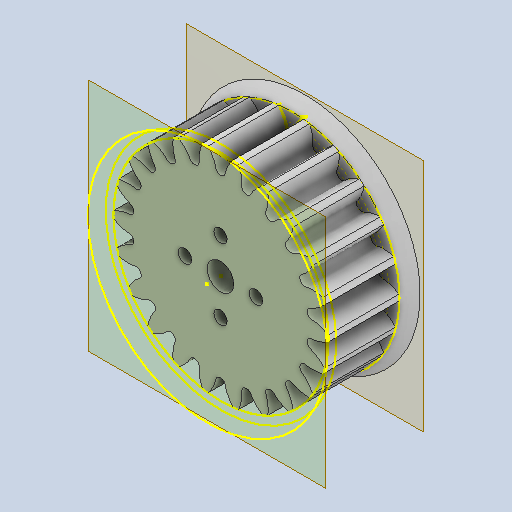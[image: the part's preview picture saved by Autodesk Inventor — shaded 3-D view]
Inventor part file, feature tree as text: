
AUTODESK INVENTOR PART (.ipt)
format: ipt  version: 2024.2 (Build 282272000, 272)  size: 422,912 bytes
history: native  units: mm
features: other x6, sketch x6
ambient origin geometry x8: Origin, YZ Plane, XZ Plane, XY Plane, X Axis, Y Axis, Z Axis, Center Point
bodies: Body1 (feature_tree)
feature tree (12):
  other  "Шест.ipt"
  other  "Твердое тело1::Шест.ipt"
  other  "Элемент создания тегов1"
  sketch  "Sketch1"  dims[d0=10.0mm]
  sketch  "Эскиз2"
  sketch  "Эскиз3"
  sketch  "Эскиз4"
  sketch  "Эскиз5"
  sketch  "Эскиз6"
  other  "РабПлоскость1"
  other  "РабПлоскость2"
  other  "Твердое тело1"
